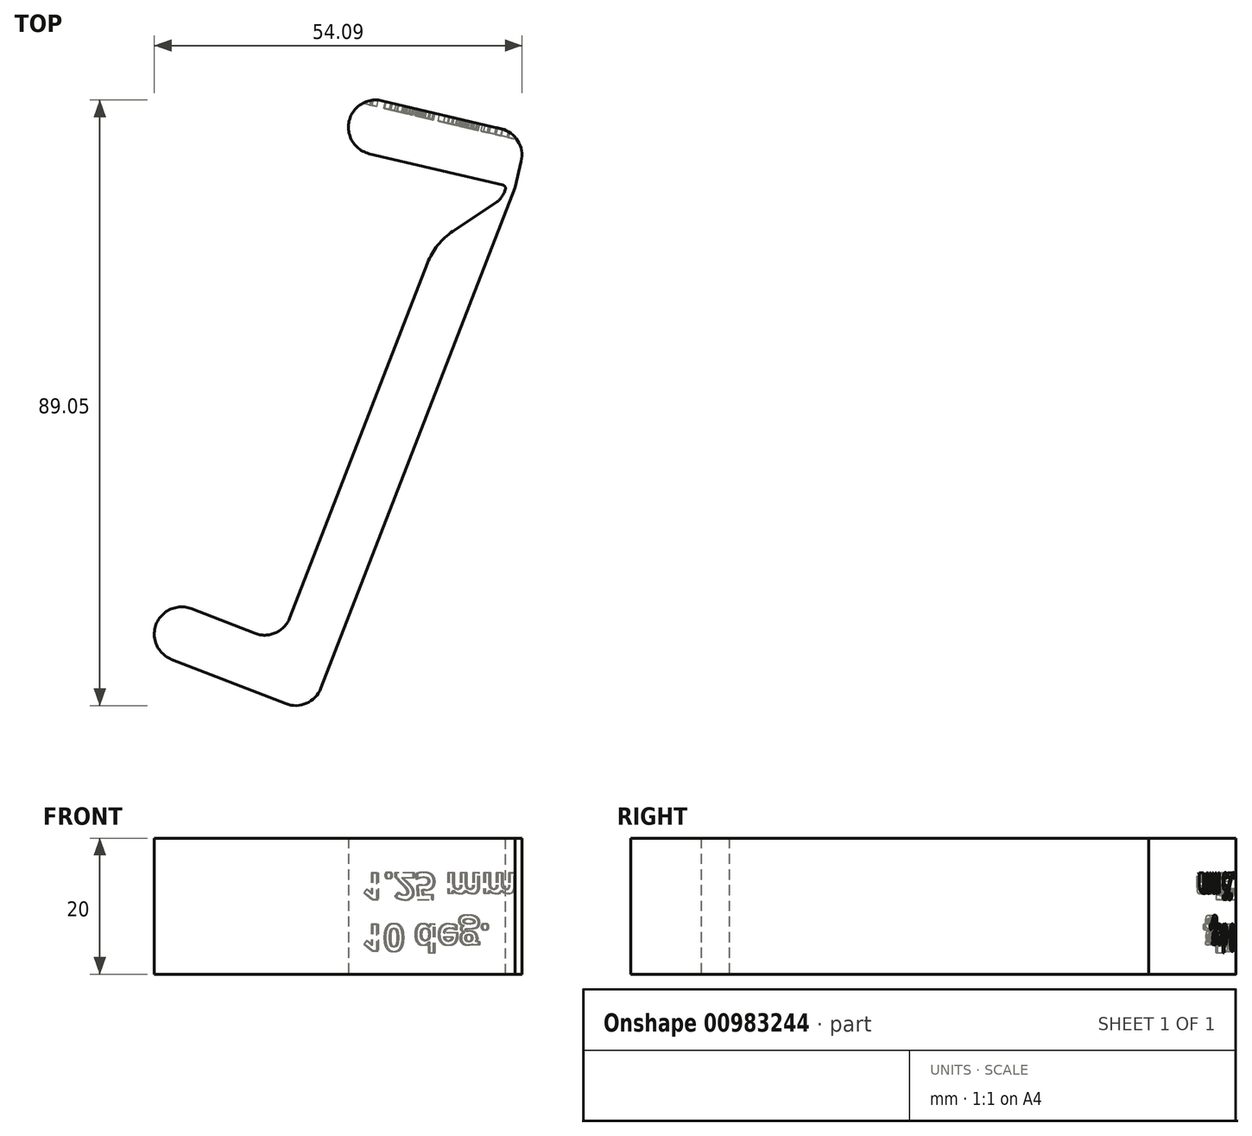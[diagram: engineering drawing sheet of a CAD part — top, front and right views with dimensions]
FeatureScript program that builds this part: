
annotation { "Feature Type Name" : "Feature", "Feature Type Description" : "" }
export const myFeature = defineFeature(function(context is Context, id is Id, definition is map)
    precondition{}
    {
        {
            var Q0;
            Q0=qCreatedBy(makeId("Top.planeOp"),FACE);
            var sketch = newSketch(context, id + "F0", { "sketchPlane" : qUnion([Q0])});
            skLineSegment(sketch, "E0", {"start": v(-18.5, -6.34) * mm, "end": v(8.64, 63.58) * mm});
            skLineSegment(sketch, "E1", {"start": v(-18.5, -6.34) * mm, "end": v(-35.28, 0.18) * mm});
            skLineSegment(sketch, "E2", {"start": v(-35.28, 0.18) * mm, "end": v(-38.17, -7.28) * mm});
            skLineSegment(sketch, "E3", {"start": v(-38.17, -7.28) * mm, "end": v(-13.93, -16.69) * mm});
            skLineSegment(sketch, "E4", {"start": v(-13.93, -16.69) * mm, "end": v(16.1, 60.69) * mm});
            skLineSegment(sketch, "E5", {"start": v(17.89, 68.4) * mm, "end": v(-21.71, 83.77) * mm});
            skLineSegment(sketch, "E6", {"start": v(17.89, 68.4) * mm, "end": v(-7.43, 74.35) * mm});
            skLineSegment(sketch, "E7", {"start": v(-7.43, 74.35) * mm, "end": v(-9.25, 66.56) * mm});
            skLineSegment(sketch, "E8", {"start": v(-9.25, 66.56) * mm, "end": v(14.84, 60.9) * mm});
            skLineSegment(sketch, "E9", {"start": v(14.84, 60.9) * mm, "end": v(14.12, 59.04) * mm});
            skLineSegment(sketch, "E10", {"start": v(14.12, 59.04) * mm, "end": v(4.34, 52.5) * mm});
            skLineSegment(sketch, "E11", {"start": v(16.1, 60.69) * mm, "end": v(17.89, 68.4) * mm});
            skSolve(sketch);
        }
        {
            var Q0;
            {var subQ5=sQuery(id+"F0.wireOp",EDGE,"E1");Q0=makeQuery(id+"F0.imprint","IMPRINT",FACE,{"disambiguationData":[TD([[makeQuery(id+"F0.imprint","IMPRINT",EDGE,{"derivedFrom":subQ5}),1.0]])]});}
            extrude(context, id + "F1", {"entities" : qUnion([Q0]), "depth" : 20 * mm, "offsetDistance" : 25 * mm});
        }
        {
            var Q0;
            Q0=makeQuery(id+"F1.opExtrude","SWEPT_FACE",FACE,{"disambiguationData":[OSD([sQuery(id+"F0.wireOp",EDGE,"E6")])]});
            var sketch = newSketch(context, id + "F2", { "sketchPlane" : qUnion([Q0])});
            skText(sketch, "E12", { "text": "10 deg.\n1.25 mm", "fontName": "OpenSans-Bold.ttf"});
            const initialGuessF2  = {"E12": [0.02302, 0.00736, -1, 0, 0.004]};
            skSetInitialGuess(sketch, initialGuessF2);
            skSolve(sketch);
        }
        {
            var Q0;
            Q0 = qSketchRegion(id + "F2", true);
            extrude(context, id + "F3", {"entities" : qUnion([Q0]), "operationType" : NewBodyOperationType.REMOVE, "oppositeDirection" : true, "depth" : 1 * mm, "offsetDistance" : 25 * mm});
        }
        {
            var Q0;
            Q0=makeQuery(id+"F1.opExtrude","SWEPT_EDGE",EDGE,{"disambiguationData":[OSD([sQuery(id+"F0.wireOp",EDGE,"E1"),sQuery(id+"F0.wireOp",EDGE,"E2")])]});
            var Q1;
            Q1=makeQuery(id+"F1.opExtrude","SWEPT_EDGE",EDGE,{"disambiguationData":[OSD([sQuery(id+"F0.wireOp",EDGE,"E2"),sQuery(id+"F0.wireOp",EDGE,"E3")])]});
            var Q2;
            Q2=makeQuery(id+"F1.opExtrude","SWEPT_EDGE",EDGE,{"disambiguationData":[OSD([sQuery(id+"F0.wireOp",EDGE,"E0"),sQuery(id+"F0.wireOp",EDGE,"E1")])]});
            var Q3;
            Q3=makeQuery(id+"F1.opExtrude","SWEPT_EDGE",EDGE,{"disambiguationData":[OSD([sQuery(id+"F0.wireOp",EDGE,"E3"),sQuery(id+"F0.wireOp",EDGE,"E4")])]});
            fillet(context, id + "F4", {"entities" : qUnion([Q0, Q1, Q2, Q3]), "radius" : 4 * mm, "tangentPropagation" : true, "allowEdgeOverflow" : false});
        }
        {
            var Q0;
            Q0=makeQuery(id+"F1.opExtrude","SWEPT_EDGE",EDGE,{"disambiguationData":[OSD([sQuery(id+"F0.wireOp",EDGE,"E0"),sQuery(id+"F0.wireOp",EDGE,"E10")])]});
            fillet(context, id + "F5", {"entities" : qUnion([Q0]), "radius" : 10 * mm, "tangentPropagation" : true, "allowEdgeOverflow" : false});
        }
        {
            var Q0;
            Q0=makeQuery(id+"F1.opExtrude","SWEPT_EDGE",EDGE,{"disambiguationData":[OSD([sQuery(id+"F0.wireOp",EDGE,"E8"),sQuery(id+"F0.wireOp",EDGE,"E9")])]});
            fillet(context, id + "F6", {"entities" : qUnion([Q0]), "radius" : 0.5 * mm, "tangentPropagation" : true, "allowEdgeOverflow" : false});
        }
        {
            var Q0;
            Q0=makeQuery(id+"F1.opExtrude","SWEPT_EDGE",EDGE,{"disambiguationData":[OSD([sQuery(id+"F0.wireOp",EDGE,"E9"),sQuery(id+"F0.wireOp",EDGE,"E10")])]});
            fillet(context, id + "F7", {"entities" : qUnion([Q0]), "radius" : 3 * mm, "tangentPropagation" : true, "allowEdgeOverflow" : false});
        }
        {
            var Q0;
            Q0=makeQuery(id+"F1.opExtrude","SWEPT_EDGE",EDGE,{"disambiguationData":[OSD([sQuery(id+"F0.wireOp",EDGE,"E7"),sQuery(id+"F0.wireOp",EDGE,"E8")])]});
            var Q1;
            Q1=makeQuery(id+"F1.opExtrude","SWEPT_EDGE",EDGE,{"disambiguationData":[OSD([sQuery(id+"F0.wireOp",EDGE,"E6"),sQuery(id+"F0.wireOp",EDGE,"E7")])]});
            var Q2;
            Q2=makeQuery(id+"F1.opExtrude","SWEPT_EDGE",EDGE,{"disambiguationData":[OSD([sQuery(id+"F0.wireOp",EDGE,"E6"),sQuery(id+"F0.wireOp",EDGE,"E11")])]});
            fillet(context, id + "F8", {"entities" : qUnion([Q0, Q1, Q2]), "radius" : 4 * mm, "tangentPropagation" : true, "allowEdgeOverflow" : false});
        }
    });
